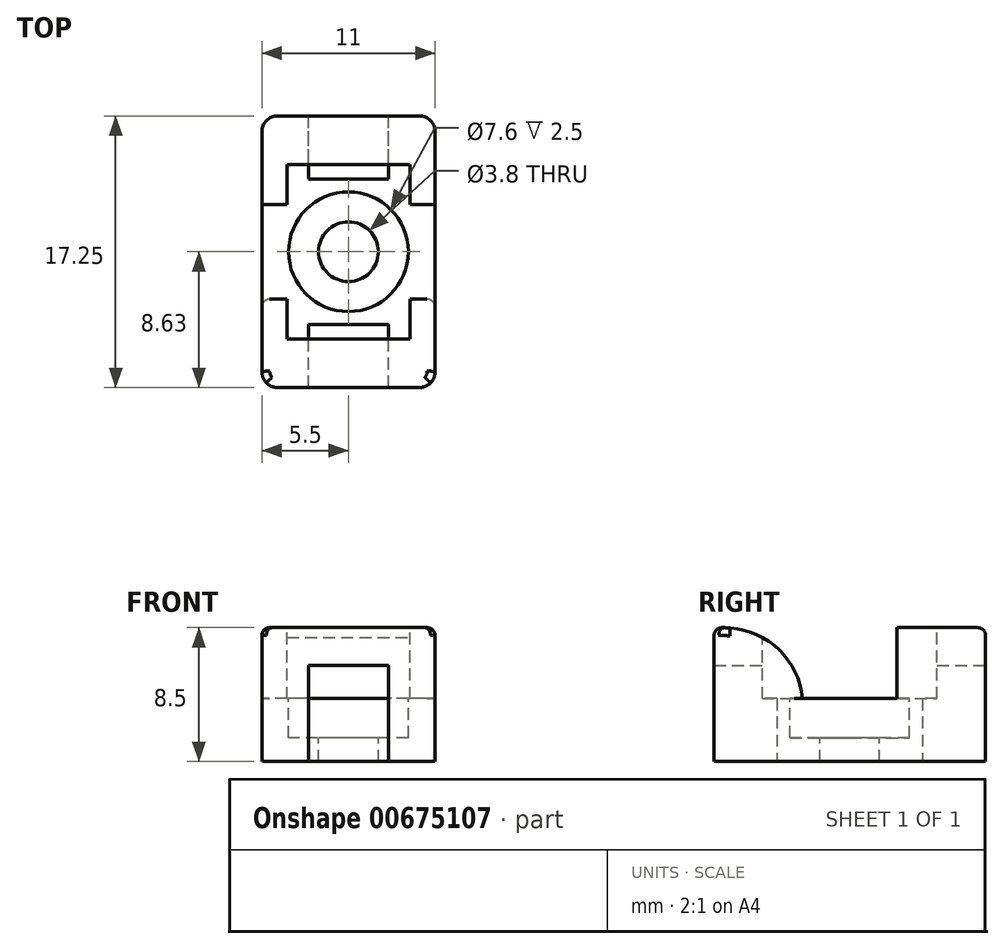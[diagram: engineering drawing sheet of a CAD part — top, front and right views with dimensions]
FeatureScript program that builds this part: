
annotation { "Feature Type Name" : "Feature", "Feature Type Description" : "" }
export const myFeature = defineFeature(function(context is Context, id is Id, definition is map)
    precondition{}
    {
        {
            var Q0;
            Q0=qCreatedBy(makeId("Top.planeOp"),FACE);
            var sketch = newSketch(context, id + "F0", { "sketchPlane" : qUnion([Q0])});
            skLineSegment(sketch, "E0.bottom", {"start": v(5.5, 8.62) * mm, "end": v(-5.5, 8.62) * mm});
            skLineSegment(sketch, "E0.top", {"start": v(5.5, -8.62) * mm, "end": v(-5.5, -8.62) * mm});
            skLineSegment(sketch, "E0.left", {"start": v(5.5, 8.62) * mm, "end": v(5.5, -8.62) * mm});
            skLineSegment(sketch, "E0.right", {"start": v(-5.5, 8.62) * mm, "end": v(-5.5, -8.62) * mm});
            skPoint(sketch, "E0.middle", {"position": v(0, 0) * mm});
            skSolve(sketch);
        }
        {
            var Q0;
            Q0 = qSketchRegion(id + "F0", true);
            extrude(context, id + "F1", {"entities" : qUnion([Q0]), "depth" : 8.5 * mm, "offsetDistance" : 25 * mm});
        }
        {
            var Q0;
            Q0=makeQuery(id+"F1.opExtrude","CAP_FACE",FACE,{"disambiguationData":[OSD([sQuery(id+"F0.wireOp",EDGE,"E0.bottom"),sQuery(id+"F0.wireOp",EDGE,"E0.top"),sQuery(id+"F0.wireOp",EDGE,"E0.left"),sQuery(id+"F0.wireOp",EDGE,"E0.right")])],"isStart":false});
            var sketch = newSketch(context, id + "F2", { "sketchPlane" : qUnion([Q0])});
            skLineSegment(sketch, "E1.bottom", {"start": v(3.9, -5.55) * mm, "end": v(-3.9, -5.55) * mm});
            skLineSegment(sketch, "E1.top", {"start": v(3.9, 5.55) * mm, "end": v(-3.9, 5.55) * mm});
            skLineSegment(sketch, "E1.left", {"start": v(3.9, -5.55) * mm, "end": v(3.9, 5.55) * mm});
            skLineSegment(sketch, "E1.right", {"start": v(-3.9, -5.55) * mm, "end": v(-3.9, 5.55) * mm});
            skPoint(sketch, "E1.middle", {"position": v(0, 0) * mm});
            skLineSegment(sketch, "E2.bottom", {"start": v(5.5, -3) * mm, "end": v(-5.5, -3) * mm});
            skLineSegment(sketch, "E2.top", {"start": v(5.5, 3) * mm, "end": v(-5.5, 3) * mm});
            skLineSegment(sketch, "E2.left", {"start": v(5.5, -3) * mm, "end": v(5.5, 3) * mm});
            skLineSegment(sketch, "E2.right", {"start": v(-5.5, -3) * mm, "end": v(-5.5, 3) * mm});
            skSolve(sketch);
        }
        {
            var Q0;
            Q0 = qSketchRegion(id + "F2", true);
            extrude(context, id + "F3", {"entities" : qUnion([Q0]), "operationType" : NewBodyOperationType.REMOVE, "oppositeDirection" : true, "depth" : 4.5 * mm, "offsetDistance" : 25 * mm});
        }
        {
            var Q0;
            Q0=makeQuery(id+"F1.opExtrude","CAP_FACE",FACE,{"disambiguationData":[OSD([sQuery(id+"F0.wireOp",EDGE,"E0.bottom"),sQuery(id+"F0.wireOp",EDGE,"E0.top"),sQuery(id+"F0.wireOp",EDGE,"E0.left"),sQuery(id+"F0.wireOp",EDGE,"E0.right")])],"isStart":true});
            var sketch = newSketch(context, id + "F4", { "sketchPlane" : qUnion([Q0])});
            skLineSegment(sketch, "E3.bottom", {"start": v(-2.55, -4.63) * mm, "end": v(2.55, -4.63) * mm});
            skLineSegment(sketch, "E3.top", {"start": v(-2.55, -8.62) * mm, "end": v(2.55, -8.62) * mm});
            skLineSegment(sketch, "E3.left", {"start": v(-2.55, -4.63) * mm, "end": v(-2.55, -8.62) * mm});
            skLineSegment(sketch, "E3.right", {"start": v(2.55, -4.63) * mm, "end": v(2.55, -8.62) * mm});
            skPoint(sketch, "E3.middle", {"position": v(0, -6.63) * mm});
            skLineSegment(sketch, "E4.bottom", {"start": v(-2.55, 8.62) * mm, "end": v(2.55, 8.62) * mm});
            skLineSegment(sketch, "E4.top", {"start": v(-2.55, 4.63) * mm, "end": v(2.55, 4.63) * mm});
            skLineSegment(sketch, "E4.left", {"start": v(-2.55, 8.62) * mm, "end": v(-2.55, 4.63) * mm});
            skLineSegment(sketch, "E4.right", {"start": v(2.55, 8.62) * mm, "end": v(2.55, 4.63) * mm});
            skPoint(sketch, "E4.middle", {"position": v(0, 6.63) * mm});
            skSolve(sketch);
        }
        {
            var Q0;
            Q0 = qSketchRegion(id + "F4", true);
            extrude(context, id + "F5", {"entities" : qUnion([Q0]), "operationType" : NewBodyOperationType.REMOVE, "oppositeDirection" : true, "depth" : 6.1 * mm, "offsetDistance" : 25 * mm});
        }
        {
            var Q0;
            Q0=makeQuery(id+"F3.boolean.opBoolean","COPY",FACE,{"derivedFrom":makeQuery(id+"F3.opExtrude","CAP_FACE",FACE,{"disambiguationData":[OSD([sQuery(id+"F2.wireOp",EDGE,"E1.bottom"),sQuery(id+"F2.wireOp",EDGE,"E1.top"),sQuery(id+"F2.wireOp",EDGE,"E1.left"),sQuery(id+"F2.wireOp",EDGE,"E1.right"),sQuery(id+"F2.wireOp",EDGE,"E2.bottom"),sQuery(id+"F2.wireOp",EDGE,"E2.top"),sQuery(id+"F2.wireOp",EDGE,"E2.left"),sQuery(id+"F2.wireOp",EDGE,"E2.right")])],"isStart":false})});
            var sketch = newSketch(context, id + "F6", { "sketchPlane" : qUnion([Q0])});
            skCircle(sketch, "E5", {"center": v(0, 0) * mm, "radius": 3.8 * mm});
            skSolve(sketch);
        }
        {
            var Q0;
            Q0 = qSketchRegion(id + "F6", true);
            extrude(context, id + "F7", {"entities" : qUnion([Q0]), "operationType" : NewBodyOperationType.REMOVE, "oppositeDirection" : true, "depth" : 2.5 * mm, "offsetDistance" : 25 * mm});
        }
        {
            var Q0;
            Q0=makeQuery(id+"F7.boolean.opBoolean","COPY",FACE,{"derivedFrom":makeQuery(id+"F7.opExtrude","CAP_FACE",FACE,{"disambiguationData":[OSD([sQuery(id+"F6.wireOp",EDGE,"E5")])],"isStart":false})});
            var sketch = newSketch(context, id + "F8", { "sketchPlane" : qUnion([Q0])});
            skCircle(sketch, "E6", {"center": v(0, 0) * mm, "radius": 1.9 * mm});
            skSolve(sketch);
        }
        {
            var Q0;
            Q0 = qSketchRegion(id + "F8", true);
            extrude(context, id + "F9", {"entities" : qUnion([Q0]), "operationType" : NewBodyOperationType.REMOVE, "endBound" : BoundingType.THROUGH_ALL, "oppositeDirection" : true, "depth" : 25 * mm, "offsetDistance" : 25 * mm});
        }
        {
            var Q0;
            {var subQ0=sQuery(id+"F2.wireOp",EDGE,"E2.bottom");Q0=makeQuery(id+"F3.boolean.opBoolean","COPY",EDGE,{"derivedFrom":makeQuery(id+"F3.opExtrude","CAP_EDGE",EDGE,{"disambiguationData":[OSD([subQ0]),TDD([makeQuery(id+"F2.imprint","IMPRINT",EDGE,{"disambiguationData":[TD([[makeQuery(id+"F2.imprint","INTERSECT",VERTEX,{"derivedFrom":[sQuery(id+"F2.wireOp",EDGE,"E1.right"),subQ0]}),-1.0]])],"derivedFrom":subQ0})])],"isStart":true})});}
            var Q1;
            {var subQ0=sQuery(id+"F2.wireOp",EDGE,"E2.top");Q1=makeQuery(id+"F3.boolean.opBoolean","COPY",EDGE,{"derivedFrom":makeQuery(id+"F3.opExtrude","CAP_EDGE",EDGE,{"disambiguationData":[OSD([subQ0]),TDD([makeQuery(id+"F2.imprint","IMPRINT",EDGE,{"disambiguationData":[TD([[makeQuery(id+"F2.imprint","INTERSECT",VERTEX,{"derivedFrom":[sQuery(id+"F2.wireOp",EDGE,"E1.right"),subQ0]}),-1.0]])],"derivedFrom":subQ0})])],"isStart":true})});}
            fillet(context, id + "F10", {"entities" : qUnion([Q0, Q1]), "radius" : 5 * mm, "tangentPropagation" : true, "allowEdgeOverflow" : false});
        }
        {
            var Q0;
            Q0=makeQuery(id+"F1.opExtrude","SWEPT_EDGE",EDGE,{"disambiguationData":[OSD([sQuery(id+"F0.wireOp",EDGE,"E0.top"),sQuery(id+"F0.wireOp",EDGE,"E0.left")])]});
            var Q1;
            Q1=makeQuery(id+"F1.opExtrude","SWEPT_EDGE",EDGE,{"disambiguationData":[OSD([sQuery(id+"F0.wireOp",EDGE,"E0.top"),sQuery(id+"F0.wireOp",EDGE,"E0.right")])]});
            var Q2;
            Q2=makeQuery(id+"F1.opExtrude","SWEPT_EDGE",EDGE,{"disambiguationData":[OSD([sQuery(id+"F0.wireOp",EDGE,"E0.bottom"),sQuery(id+"F0.wireOp",EDGE,"E0.left")])]});
            var Q3;
            Q3=makeQuery(id+"F1.opExtrude","SWEPT_EDGE",EDGE,{"disambiguationData":[OSD([sQuery(id+"F0.wireOp",EDGE,"E0.bottom"),sQuery(id+"F0.wireOp",EDGE,"E0.right")])]});
            fillet(context, id + "F11", {"entities" : qUnion([Q0, Q1, Q2, Q3]), "radius" : 1 * mm, "tangentPropagation" : true, "allowEdgeOverflow" : false});
        }
        {
            var Q0;
            Q0=makeQuery(id+"F1.opExtrude","CAP_EDGE",EDGE,{"disambiguationData":[OSD([sQuery(id+"F0.wireOp",EDGE,"E0.bottom")])],"isStart":false});
            var Q1;
            Q1=makeQuery(id+"F1.opExtrude","CAP_EDGE",EDGE,{"disambiguationData":[OSD([sQuery(id+"F0.wireOp",EDGE,"E0.top")])],"isStart":false});
            var Q2;
            Q2=makeQuery(id+"F3.boolean.opBoolean","COPY",EDGE,{"derivedFrom":makeQuery(id+"F3.opExtrude","CAP_EDGE",EDGE,{"disambiguationData":[OSD([sQuery(id+"F2.wireOp",EDGE,"E2.right")])],"isStart":false})});
            var Q3;
            Q3=makeQuery(id+"F3.boolean.opBoolean","COPY",EDGE,{"derivedFrom":makeQuery(id+"F3.opExtrude","CAP_EDGE",EDGE,{"disambiguationData":[OSD([sQuery(id+"F2.wireOp",EDGE,"E2.left")])],"isStart":false})});
            fillet(context, id + "F12", {"entities" : qUnion([Q0, Q1, Q2, Q3]), "radius" : .5 * mm, "tangentPropagation" : true, "allowEdgeOverflow" : false});
        }
    });
